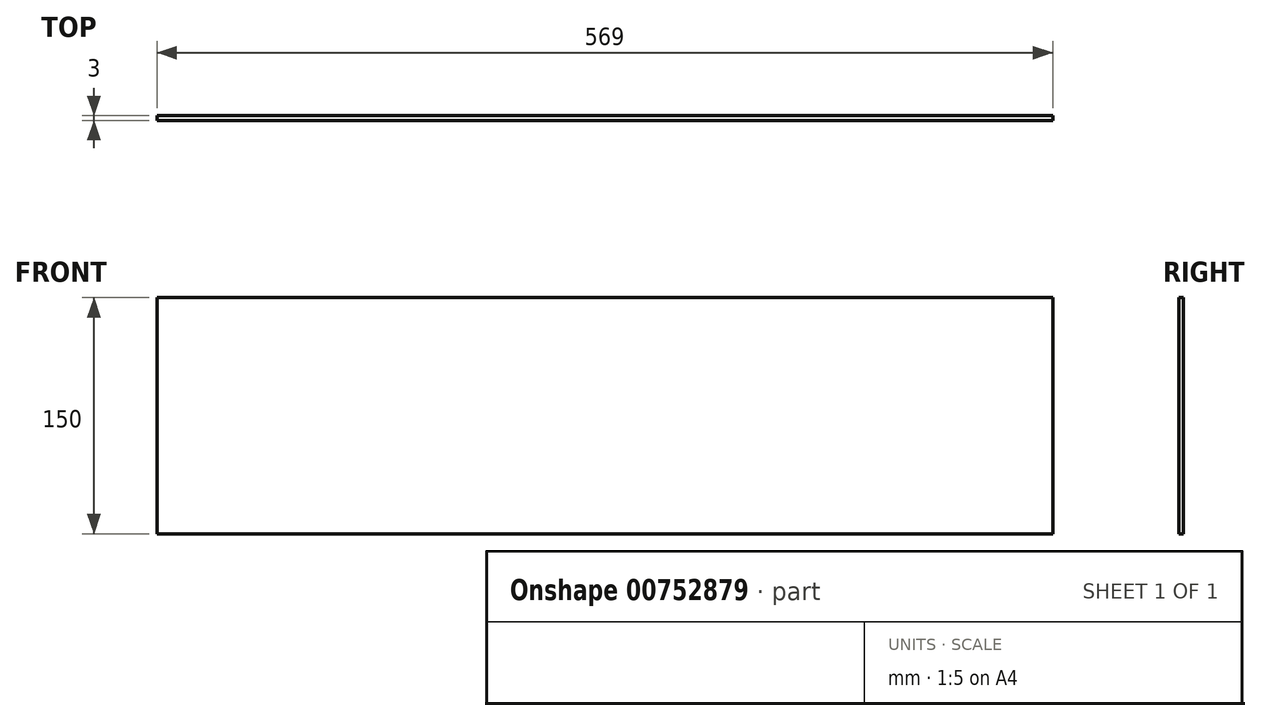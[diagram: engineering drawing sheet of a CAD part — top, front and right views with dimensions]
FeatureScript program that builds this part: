
annotation { "Feature Type Name" : "Feature", "Feature Type Description" : "" }
export const myFeature = defineFeature(function(context is Context, id is Id, definition is map)
    precondition{}
    {
        {
            var Q0;
            Q0=qCreatedBy(makeId("Front.planeOp"),FACE);
            var sketch = newSketch(context, id + "F0", { "sketchPlane" : qUnion([Q0])});
            skLineSegment(sketch, "E0.bottom", {"start": v(-284.5, 75) * mm, "end": v(284.5, 75) * mm});
            skLineSegment(sketch, "E0.top", {"start": v(-284.5, -75) * mm, "end": v(284.5, -75) * mm});
            skLineSegment(sketch, "E0.left", {"start": v(-284.5, 75) * mm, "end": v(-284.5, -75) * mm});
            skLineSegment(sketch, "E0.right", {"start": v(284.5, 75) * mm, "end": v(284.5, -75) * mm});
            skPoint(sketch, "E0.middle", {"position": v(0, 0) * mm});
            skSolve(sketch);
        }
        {
            var Q0;
            Q0=makeQuery(id+"F0.imprint","IMPRINT",FACE,{"disambiguationData":[TD([[makeQuery(id+"F0.imprint","IMPRINT",EDGE,{"derivedFrom":sQuery(id+"F0.wireOp",EDGE,"E0.bottom")}),-1.0]])]});
            extrude(context, id + "F1", {"entities" : qUnion([Q0]), "depth" : 3 * mm, "offsetDistance" : 25 * mm});
        }
    });
